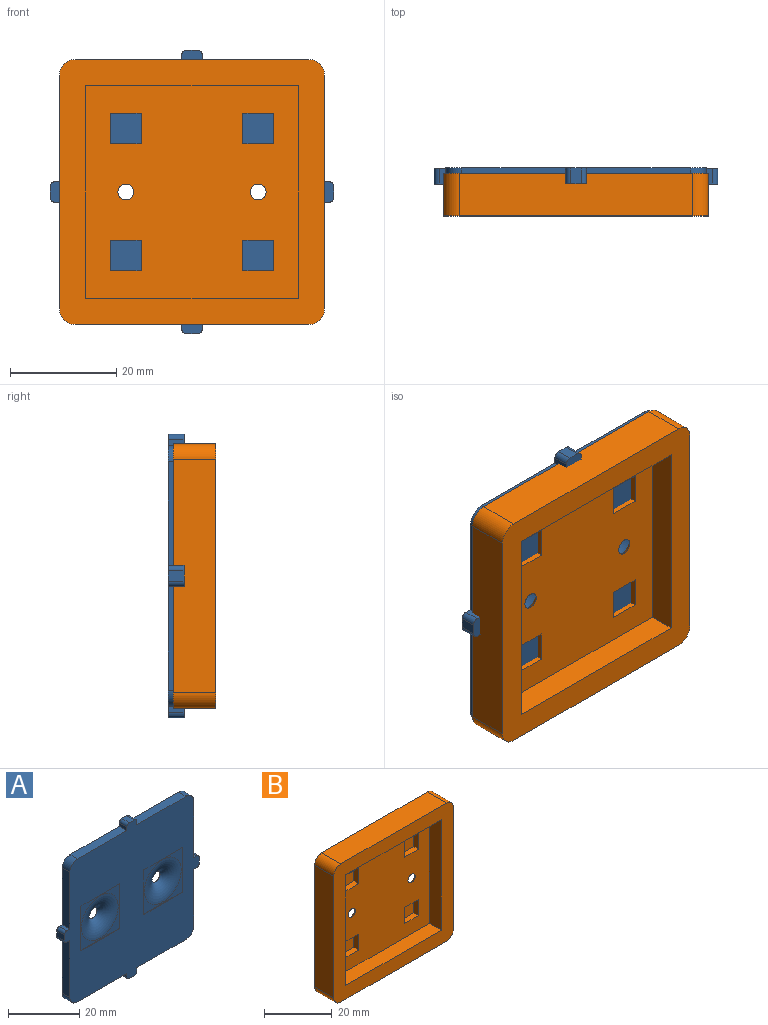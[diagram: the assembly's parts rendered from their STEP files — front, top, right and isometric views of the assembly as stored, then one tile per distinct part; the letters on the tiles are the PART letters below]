
ASSEMBLY  parts=2 mates=1
PART A: 66 faces, bbox 53.5x7.2x53.5 mm
  f0: plane 53.5x53.5mm, normal (0,-1,0), area 1962.2mm2, adj f2,f3,f4,f5,f6,f7,f8,f9
  f1: plane 53.5x53.5mm, normal (0,1,0), area 2283.8mm2, adj f2,f3,f4,f5,f6,f7,f8,f9
  f2: plane 3x1.2mm, normal (-1,0,0), area 3.6mm2, adj f0,f1,f3,f59
  f3: plane 19.55x3mm, normal (0,0,1), area 58.6mm2, adj f0,f1,f2,f24
  f4: plane 19.55x3mm, normal (-1,0,0), area 58.6mm2, adj f0,f1,f5,f24
  f5: plane 3x1.2mm, normal (0,0,1), area 3.6mm2, adj f0,f1,f4,f60
  f6: plane 3x2mm, normal (-1,0,0), area 6mm2, adj f0,f1,f60,f61
  f7: plane 3x1.2mm, normal (0,0,-1), area 3.6mm2, adj f0,f1,f8,f61
  f8: plane 19.55x3mm, normal (-1,0,0), area 58.6mm2, adj f0,f1,f7,f25
  f9: plane 19.55x3mm, normal (0,0,-1), area 58.6mm2, adj f0,f1,f10,f25
  f10: plane 3x1.2mm, normal (-1,0,0), area 3.6mm2, adj f0,f1,f9,f62
  f11: plane 3x2mm, normal (0,0,-1), area 6mm2, adj f0,f1,f62,f63
  f12: plane 3x1.2mm, normal (1,0,0), area 3.6mm2, adj f0,f1,f13,f63
  f13: plane 19.55x3mm, normal (0,0,-1), area 58.6mm2, adj f0,f1,f12,f22
  f14: plane 19.55x3mm, normal (1,0,0), area 58.6mm2, adj f0,f1,f15,f22
  f15: plane 3x1.2mm, normal (0,0,-1), area 3.6mm2, adj f0,f1,f14,f64
  f16: plane 3x2mm, normal (1,0,0), area 6mm2, adj f0,f1,f64,f65
  f17: plane 3x1.2mm, normal (0,0,1), area 3.6mm2, adj f0,f1,f18,f65
  f18: plane 19.55x3mm, normal (1,0,0), area 58.6mm2, adj f0,f1,f17,f23
  f19: plane 19.55x3mm, normal (0,0,1), area 58.6mm2, adj f0,f1,f20,f23
  f20: plane 3x1.2mm, normal (1,0,0), area 3.6mm2, adj f0,f1,f19,f58
  f21: plane 3x2mm, normal (0,0,1), area 6mm2, adj f0,f1,f58,f59
  f22: cylinder r=3mm len=3mm, axis (0,-1,0), area 14.1mm2, adj f0,f1,f13,f14
  f23: cylinder r=3mm len=3mm, axis (0,1,0), area 14.1mm2, adj f0,f1,f18,f19
  f24: cylinder r=3mm len=3mm, axis (0,-1,0), area 14.1mm2, adj f0,f1,f3,f4
  f25: cylinder r=3mm len=3mm, axis (0,1,0), area 14.1mm2, adj f0,f1,f8,f9
  f26: plane 5.8x2mm, normal (0,0,1), area 11.6mm2, adj f1,f27,f29,f30
  f27: plane 5.8x2mm, normal (1,0,0), area 11.6mm2, adj f1,f26,f28,f30
  f28: plane 5.8x2mm, normal (0,0,-1), area 11.6mm2, adj f1,f27,f29,f30
  f29: plane 5.8x2mm, normal (-1,0,0), area 11.6mm2, adj f1,f26,f28,f30
  f30: plane 5.8x5.8mm, normal (0,1,0), area 33.6mm2, adj f26,f27,f28,f29
  f31: plane 5.8x2mm, normal (0,0,1), area 11.6mm2, adj f1,f32,f34,f35
  f32: plane 5.8x2mm, normal (1,0,0), area 11.6mm2, adj f1,f31,f33,f35
  f33: plane 5.8x2mm, normal (0,0,-1), area 11.6mm2, adj f1,f32,f34,f35
  f34: plane 5.8x2mm, normal (-1,0,0), area 11.6mm2, adj f1,f31,f33,f35
  f35: plane 5.8x5.8mm, normal (0,1,0), area 33.6mm2, adj f31,f32,f33,f34
  f36: plane 5.8x2mm, normal (0,0,1), area 11.6mm2, adj f1,f37,f39,f40
  f37: plane 5.8x2mm, normal (1,0,0), area 11.6mm2, adj f1,f36,f38,f40
  f38: plane 5.8x2mm, normal (0,0,-1), area 11.6mm2, adj f1,f37,f39,f40
  f39: plane 5.8x2mm, normal (-1,0,0), area 11.6mm2, adj f1,f36,f38,f40
  f40: plane 5.8x5.8mm, normal (0,1,0), area 33.6mm2, adj f36,f37,f38,f39
  f41: plane 5.8x2mm, normal (0,0,1), area 11.6mm2, adj f1,f42,f44,f45
  f42: plane 5.8x2mm, normal (1,0,0), area 11.6mm2, adj f1,f41,f43,f45
  f43: plane 5.8x2mm, normal (0,0,-1), area 11.6mm2, adj f1,f42,f44,f45
  f44: plane 5.8x2mm, normal (-1,0,0), area 11.6mm2, adj f1,f41,f43,f45
  f45: plane 5.8x5.8mm, normal (0,1,0), area 33.6mm2, adj f41,f42,f43,f44
  f46: plane 15.4x0.2mm, normal (0,0,-1), area 3.1mm2, adj f0,f47,f49,f50
  f47: plane 15.4x0.2mm, normal (1,0,0), area 3.1mm2, adj f0,f46,f48,f50
  f48: plane 15.4x0.2mm, normal (0,0,1), area 3.1mm2, adj f0,f47,f49,f50
  f49: plane 15.4x0.2mm, normal (-1,0,0), area 3.1mm2, adj f0,f46,f48,f50
  f50: plane 15.4x15.4mm, normal (0,-1,0), area 69.7mm2, adj f46,f47,f48,f49,f57
  f51: plane 15.4x0.2mm, normal (0,0,-1), area 3.1mm2, adj f0,f52,f54,f55
  f52: plane 15.4x0.2mm, normal (1,0,0), area 3.1mm2, adj f0,f51,f53,f55
  f53: plane 15.4x0.2mm, normal (0,0,1), area 3.1mm2, adj f0,f52,f54,f55
  f54: plane 15.4x0.2mm, normal (-1,0,0), area 3.1mm2, adj f0,f51,f53,f55
  f55: plane 15.4x15.4mm, normal (0,-1,0), area 69.7mm2, adj f51,f52,f53,f54,f56
  f56: torus R=7.3mm, axis (0,-1,0), area 174.6mm2, adj f1,f55
  f57: torus R=7.3mm, axis (0,-1,0), area 174.6mm2, adj f1,f50
  f58: cylinder r=1mm len=3mm, axis (0,-1,0), area 4.7mm2, adj f0,f1,f20,f21
  f59: cylinder r=1mm len=3mm, axis (0,1,0), area 4.7mm2, adj f0,f1,f2,f21
  f60: cylinder r=1mm len=3mm, axis (0,-1,0), area 4.7mm2, adj f0,f1,f5,f6
  f61: cylinder r=1mm len=3mm, axis (0,1,0), area 4.7mm2, adj f0,f1,f6,f7
  f62: cylinder r=1mm len=3mm, axis (0,1,0), area 4.7mm2, adj f0,f1,f10,f11
  f63: cylinder r=1mm len=3mm, axis (0,-1,0), area 4.7mm2, adj f0,f1,f11,f12
  f64: cylinder r=1mm len=3mm, axis (0,-1,0), area 4.7mm2, adj f0,f1,f15,f16
  f65: cylinder r=1mm len=3mm, axis (0,1,0), area 4.7mm2, adj f0,f1,f16,f17
PART B: 47 faces, bbox 50x15.1x50 mm
  f0: plane 40x40mm, normal (0,-1,0), area 1451.3mm2, adj f6,f7,f8,f9,f25,f26,f27,f28
  f1: plane 50x50mm, normal (0,1,0), area 2018mm2, adj f2,f3,f4,f5,f11,f12,f13,f14
  f2: plane 44x8mm, normal (0,0,1), area 352mm2, adj f1,f10,f21,f24
  f3: plane 44x8mm, normal (-1,0,0), area 352mm2, adj f1,f10,f21,f22
  f4: plane 44x8mm, normal (0,0,-1), area 352mm2, adj f1,f10,f22,f23
  f5: plane 44x8mm, normal (1,0,0), area 352mm2, adj f1,f10,f23,f24
  f6: plane 40x5mm, normal (1,0,0), area 200mm2, adj f0,f7,f9,f10
  f7: plane 40x5mm, normal (0,0,-1), area 200mm2, adj f0,f6,f8,f10
  f8: plane 40x5mm, normal (-1,0,0), area 200mm2, adj f0,f7,f9,f10
  f9: plane 40x5mm, normal (0,0,1), area 200mm2, adj f0,f6,f8,f10
  f10: plane 50x50mm, normal (0,-1,0), area 892.3mm2, adj f2,f3,f4,f5,f6,f7,f8,f9
  f11: plane 15.4x0.2mm, normal (0,0,-1), area 3.1mm2, adj f1,f12,f14,f15
  f12: plane 15.4x0.2mm, normal (-1,0,0), area 3.1mm2, adj f1,f11,f13,f15
  f13: plane 15.4x0.2mm, normal (0,0,1), area 3.1mm2, adj f1,f12,f14,f15
  f14: plane 15.4x0.2mm, normal (1,0,0), area 3.1mm2, adj f1,f11,f13,f15
  f15: plane 15.4x15.4mm, normal (0,1,0), area 67.7mm2, adj f11,f12,f13,f14,f45
  f16: plane 15.4x0.2mm, normal (0,0,-1), area 3.1mm2, adj f1,f17,f19,f20
  f17: plane 15.4x0.2mm, normal (-1,0,0), area 3.1mm2, adj f1,f16,f18,f20
  f18: plane 15.4x0.2mm, normal (0,0,1), area 3.1mm2, adj f1,f17,f19,f20
  f19: plane 15.4x0.2mm, normal (1,0,0), area 3.1mm2, adj f1,f16,f18,f20
  f20: plane 15.4x15.4mm, normal (0,1,0), area 67.7mm2, adj f16,f17,f18,f19,f46
  f21: cylinder r=3mm len=8mm, axis (0,-1,0), area 37.7mm2, adj f1,f2,f3,f10
  f22: cylinder r=3mm len=8mm, axis (0,1,0), area 37.7mm2, adj f1,f3,f4,f10
  f23: cylinder r=3mm len=8mm, axis (0,-1,0), area 37.7mm2, adj f1,f4,f5,f10
  f24: cylinder r=3mm len=8mm, axis (0,1,0), area 37.7mm2, adj f1,f2,f5,f10
  f25: plane 5.8x2mm, normal (0,0,1), area 11.6mm2, adj f0,f26,f28,f29
  f26: plane 5.8x2mm, normal (-1,0,0), area 11.6mm2, adj f0,f25,f27,f29
  f27: plane 5.8x2mm, normal (0,0,-1), area 11.6mm2, adj f0,f26,f28,f29
  f28: plane 5.8x2mm, normal (1,0,0), area 11.6mm2, adj f0,f25,f27,f29
  f29: plane 5.8x5.8mm, normal (0,-1,0), area 33.6mm2, adj f25,f26,f27,f28
  f30: plane 5.8x2mm, normal (0,0,1), area 11.6mm2, adj f0,f31,f33,f34
  f31: plane 5.8x2mm, normal (-1,0,0), area 11.6mm2, adj f0,f30,f32,f34
  f32: plane 5.8x2mm, normal (0,0,-1), area 11.6mm2, adj f0,f31,f33,f34
  f33: plane 5.8x2mm, normal (1,0,0), area 11.6mm2, adj f0,f30,f32,f34
  f34: plane 5.8x5.8mm, normal (0,-1,0), area 33.6mm2, adj f30,f31,f32,f33
  f35: plane 5.8x2mm, normal (0,0,1), area 11.6mm2, adj f0,f36,f38,f39
  f36: plane 5.8x2mm, normal (-1,0,0), area 11.6mm2, adj f0,f35,f37,f39
  f37: plane 5.8x2mm, normal (0,0,-1), area 11.6mm2, adj f0,f36,f38,f39
  f38: plane 5.8x2mm, normal (1,0,0), area 11.6mm2, adj f0,f35,f37,f39
  f39: plane 5.8x5.8mm, normal (0,-1,0), area 33.6mm2, adj f35,f36,f37,f38
  f40: plane 5.8x2mm, normal (0,0,1), area 11.6mm2, adj f0,f41,f43,f44
  f41: plane 5.8x2mm, normal (-1,0,0), area 11.6mm2, adj f0,f40,f42,f44
  f42: plane 5.8x2mm, normal (0,0,-1), area 11.6mm2, adj f0,f41,f43,f44
  f43: plane 5.8x2mm, normal (1,0,0), area 11.6mm2, adj f0,f40,f42,f44
  f44: plane 5.8x5.8mm, normal (0,-1,0), area 33.6mm2, adj f40,f41,f42,f43
  f45: torus R=7.34mm, axis (0,1,0), area 177.3mm2, adj f0,f15
  f46: torus R=7.34mm, axis (0,1,0), area 177.3mm2, adj f0,f20
PLACE A t=(-76.14,-19.32,10.05)mm
PLACE B t=(-82.61,-20.32,-5.25)mm
MATE fastened B.f34 <-> A.f35  axis (0,-1,0) through (-63.64,-21.32,22.05)mm
